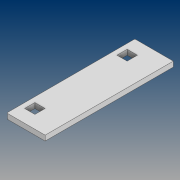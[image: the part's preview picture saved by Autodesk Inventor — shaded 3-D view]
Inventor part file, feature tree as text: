
AUTODESK INVENTOR PART (.ipt)
format: ipt  version: 2021 (Build 250183000, 183)  size: 100,352 bytes
history: native  units: mm
features: extrude x1, fillet x1, sketch x1
ambient origin geometry x8: Origin, YZ Plane, XZ Plane, XY Plane, X Axis, Y Axis, Z Axis, Center Point
bodies: Solid1 (feature_tree)
feature tree (3):
  extrude  "Extrusion1"  Depth=2.0mm
  fillet  "Fillet1"  Radius=180.0mm
  sketch  "Sketch1"  dims[d0=250.0mm d1=40.0mm d2=180.0mm d3=20.0mm d4=35.0mm d5=10.0mm d6=0.0mm d7=2.0mm]
